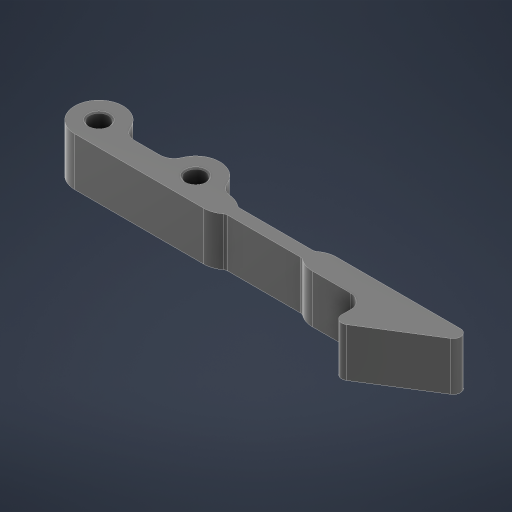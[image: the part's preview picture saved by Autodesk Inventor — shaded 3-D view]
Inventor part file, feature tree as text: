
AUTODESK INVENTOR PART (.ipt)
format: ipt  version: 2025 (Build 290162010, 162A)  size: 266,240 bytes
history: native  units: mm
features: sketch x3, extrude x2, chamfer x1, fillet x1, projected_geometry x1
ambient origin geometry x8: Origin, YZ Plane, XZ Plane, XY Plane, X Axis, Y Axis, Z Axis, Center Point
bodies: Solid1 (feature_tree)
feature tree (8):
  extrude  "Extrusion1"  Depth=4.0mm
  chamfer  "Chamfer1"  Distance=3.0mm
  sketch  "Sketch2"  dims[d5=10.0mm]
  extrude  "Extrusion2"  Depth=5.0mm
  fillet  "Fillet2"  Radius=12.5mm
  sketch  "Sketch1"  dims[d0=4.0mm d4=4.0mm]
  projected_geometry  "Projected Loop1"
  sketch  "Sketch3"  dims[d6=10.0mm d7=3.0mm d8=80.0mm d9=12.5mm d10=20.0mm d11=60.0mm d12=3.0mm d13=1.5mm d14=10.0mm d15=0.0mm d16=0.25mm d17=2.0mm d18=45.0deg d19=5.0mm d20=3.0mm d21=3.0mm d22=5.0mm d25=0.0mm d26=0.0mm d28=15.0mm d29=2.5mm d30=15.0mm d31=2.5mm d32=5.0mm]
